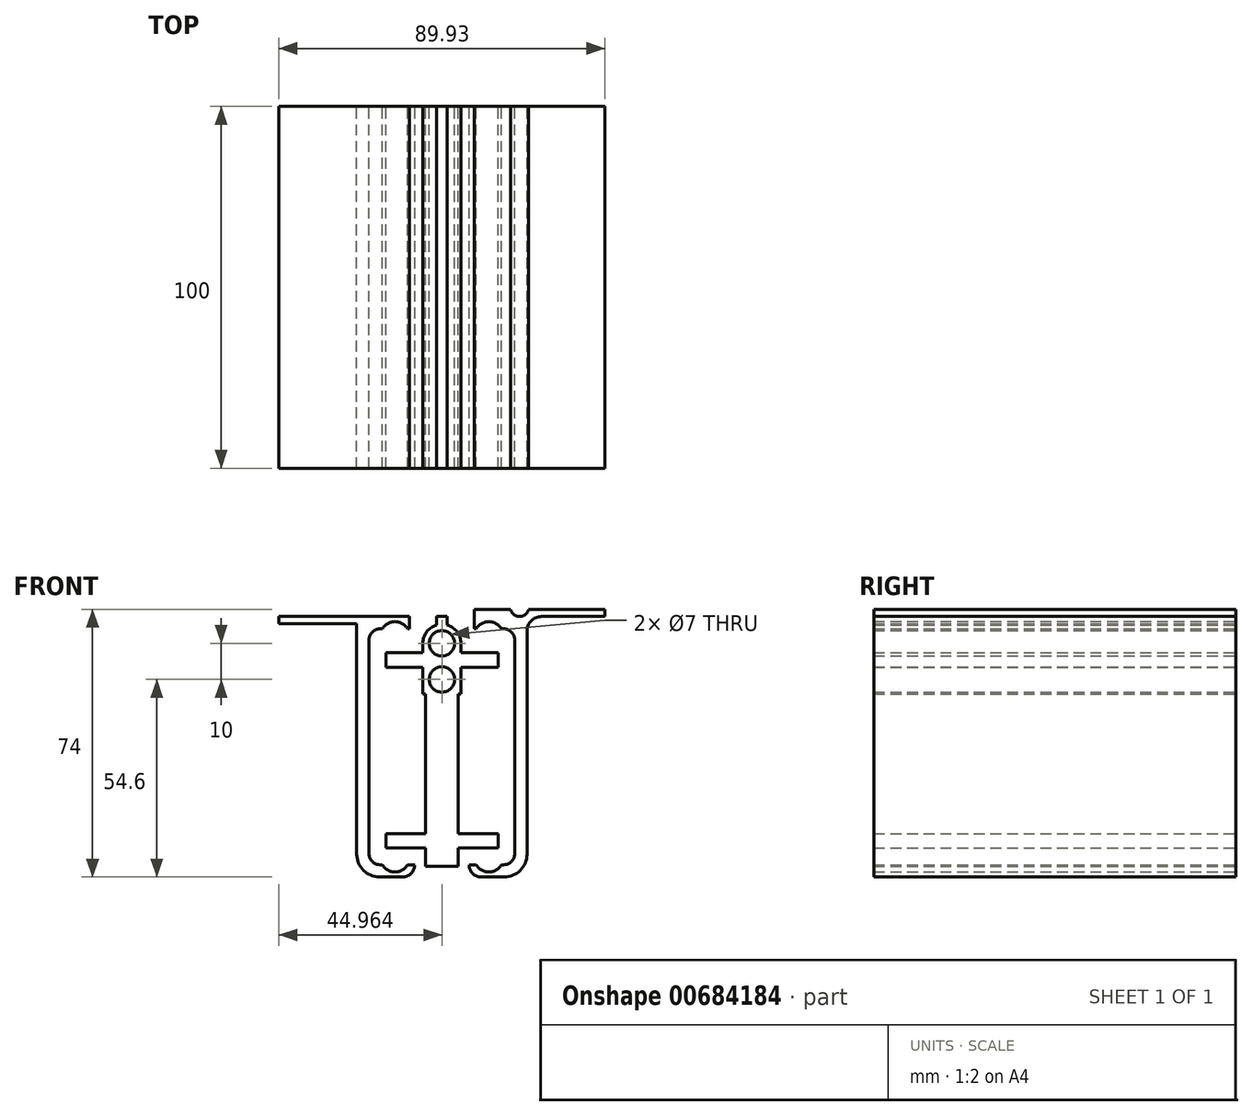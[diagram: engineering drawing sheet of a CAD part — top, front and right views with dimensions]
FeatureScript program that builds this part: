
annotation { "Feature Type Name" : "Feature", "Feature Type Description" : "" }
export const myFeature = defineFeature(function(context is Context, id is Id, definition is map)
    precondition{}
    {
        {
            var Q0;
            Q0=qCreatedBy(makeId("Front.planeOp"),FACE);
            var sketch = newSketch(context, id + "F0", { "sketchPlane" : qUnion([Q0])});
            skLineSegment(sketch, "E0", {"start": v(67.58, 68) * mm, "end": v(67.58, 6.3) * mm});
            skLineSegment(sketch, "E1", {"start": v(71.58, 72) * mm, "end": v(89.05, 72) * mm});
            skArc(sketch, "E2.filletArc", {"start": v(71.58, 72) * mm, "mid": v(68.76, 70.83) * mm, "end": v(67.58, 68) * mm});
            skLineSegment(sketch, "E3", {"start": v(61.18, 68.6) * mm, "end": v(53.05, 68.6) * mm});
            skLineSegment(sketch, "E4", {"start": v(61.18, 3.4) * mm, "end": v(51.58, 3.4) * mm});
            skLineSegment(sketch, "E5.0", {"start": v(64.18, 65.6) * mm, "end": v(64.18, 6.4) * mm});
            skArc(sketch, "E6.filletArc", {"start": v(61.18, 3.4) * mm, "mid": v(63.3, 4.28) * mm, "end": v(64.18, 6.4) * mm});
            skArc(sketch, "E7.filletArc", {"start": v(64.18, 65.6) * mm, "mid": v(63.3, 67.72) * mm, "end": v(61.18, 68.6) * mm});
            skLineSegment(sketch, "E8", {"start": v(61.28, 0) * mm, "end": v(54.98, 0) * mm});
            skPoint(sketch, "E9.visualSharp", {"position": v(67.58, 0) * mm});
            skArc(sketch, "E9.filletArc", {"start": v(61.28, 0) * mm, "mid": v(65.74, 1.85) * mm, "end": v(67.58, 6.3) * mm});
            skArc(sketch, "E10", {"start": v(60.51, 68.6) * mm, "mid": v(57.05, 70.6) * mm, "end": v(53.58, 68.6) * mm});
            skLineSegment(sketch, "E11", {"start": v(53.05, 68.6) * mm, "end": v(53.05, 74) * mm});
            skArc(sketch, "E12", {"start": v(63.05, 74) * mm, "mid": v(65.55, 72) * mm, "end": v(68.05, 74) * mm});
            skLineSegment(sketch, "E13", {"start": v(53.05, 74) * mm, "end": v(89.05, 74) * mm});
            skLineSegment(sketch, "E14", {"start": v(89.05, 72) * mm, "end": v(89.05, 74) * mm});
            skPoint(sketch, "E15", {"position": v(65.55, 72) * mm});
            skPoint(sketch, "E16", {"position": v(57.05, 70.6) * mm});
            skLineSegment(sketch, "E17", {"start": v(51.58, 3.4) * mm, "end": v(51.58, 3.4) * mm});
            skArc(sketch, "E18", {"start": v(53.58, 3.4) * mm, "mid": v(57.05, 1.4) * mm, "end": v(60.51, 3.4) * mm});
            skPoint(sketch, "E19", {"position": v(57.05, 1.4) * mm});
            skLineSegment(sketch, "E20", {"start": v(57.05, 66.6) * mm, "end": v(57.05, 5.3) * mm, "construction": true});
            skPoint(sketch, "E21.visualSharp", {"position": v(51.58, 0) * mm});
            skArc(sketch, "E21.filletArc", {"start": v(51.58, 3.4) * mm, "mid": v(52.58, 1) * mm, "end": v(54.98, 0) * mm});
            skLineSegment(sketch, "E22", {"start": v(44.08, 80.45) * mm, "end": v(44.08, 38.77) * mm, "construction": true});
            skLineSegment(sketch, "E23.MirrorCS", {"start": v(23.98, 65.6) * mm, "end": v(23.98, 6.4) * mm});
            skArc(sketch, "E24.MirrorCS", {"start": v(23.98, 65.6) * mm, "mid": v(24.86, 67.72) * mm, "end": v(26.98, 68.6) * mm});
            skArc(sketch, "E25.MirrorCS", {"start": v(26.98, 3.4) * mm, "mid": v(24.86, 4.28) * mm, "end": v(23.98, 6.4) * mm});
            skArc(sketch, "E26.MirrorCS", {"start": v(27.66, 68.6) * mm, "mid": v(31.12, 70.6) * mm, "end": v(34.58, 68.6) * mm});
            skLineSegment(sketch, "E27.MirrorCS", {"start": v(26.98, 68.6) * mm, "end": v(35.12, 68.6) * mm});
            skLineSegment(sketch, "E28.MirrorCS", {"start": v(26.98, 3.4) * mm, "end": v(36.58, 3.4) * mm});
            skArc(sketch, "E29.MirrorCS", {"start": v(34.58, 3.4) * mm, "mid": v(31.12, 1.4) * mm, "end": v(27.66, 3.4) * mm});
            skArc(sketch, "E30.MirrorCS", {"start": v(36.58, 3.4) * mm, "mid": v(35.59, 1) * mm, "end": v(33.18, 0) * mm});
            skLineSegment(sketch, "E31.MirrorCS", {"start": v(26.88, 0) * mm, "end": v(33.18, 0) * mm});
            skArc(sketch, "E32.MirrorCS", {"start": v(26.88, 0) * mm, "mid": v(22.43, 1.85) * mm, "end": v(20.58, 6.3) * mm});
            skLineSegment(sketch, "E33", {"start": v(20.58, 6.3) * mm, "end": v(20.58, 70) * mm});
            skLineSegment(sketch, "E34", {"start": v(20.58, 70) * mm, "end": v(-0.88, 70) * mm});
            skLineSegment(sketch, "E35", {"start": v(-0.88, 70) * mm, "end": v(-0.88, 72) * mm});
            skLineSegment(sketch, "E36", {"start": v(-0.88, 72) * mm, "end": v(35.12, 72) * mm});
            skLineSegment(sketch, "E37", {"start": v(35.12, 72) * mm, "end": v(35.12, 68.6) * mm});
            skCircle(sketch, "E38", {"center": v(44.08, 64.6) * mm, "radius": 3.5 * mm});
            skCircle(sketch, "E39", {"center": v(44.08, 54.6) * mm, "radius": 3.5 * mm});
            skLineSegment(sketch, "E40.top", {"start": v(38.83, 50.6) * mm, "end": v(39.58, 50.6) * mm});
            skLineSegment(sketch, "E40.left", {"start": v(38.83, 64.6) * mm, "end": v(38.83, 62) * mm});
            skLineSegment(sketch, "E40.right", {"start": v(49.33, 64.6) * mm, "end": v(49.33, 62) * mm});
            skLineSegment(sketch, "E41.bottom", {"start": v(39.58, 3) * mm, "end": v(48.58, 3) * mm});
            skLineSegment(sketch, "E41.left", {"start": v(39.58, 3) * mm, "end": v(39.58, 8) * mm});
            skLineSegment(sketch, "E41.right", {"start": v(48.58, 3) * mm, "end": v(48.58, 8) * mm});
            skLineSegment(sketch, "E42.trimOffspring", {"start": v(48.58, 50.6) * mm, "end": v(49.33, 50.6) * mm});
            skCircle(sketch, "E43.0", {"center": v(44.08, 64.6) * mm, "radius": 5.25 * mm});
            skLineSegment(sketch, "E44.bottom", {"start": v(45.58, 72) * mm, "end": v(42.58, 72) * mm});
            skLineSegment(sketch, "E44.left", {"start": v(45.58, 72) * mm, "end": v(45.58, 69.63) * mm});
            skLineSegment(sketch, "E44.right", {"start": v(42.58, 72) * mm, "end": v(42.58, 69.63) * mm});
            skLineSegment(sketch, "E45.bottom", {"start": v(28.58, 8) * mm, "end": v(39.58, 8) * mm});
            skLineSegment(sketch, "E45.top", {"start": v(28.58, 12) * mm, "end": v(39.58, 12) * mm});
            skLineSegment(sketch, "E45.left", {"start": v(28.58, 8) * mm, "end": v(28.58, 12) * mm});
            skLineSegment(sketch, "E45.right", {"start": v(59.58, 8) * mm, "end": v(59.58, 12) * mm});
            skLineSegment(sketch, "E46.trimOffspring", {"start": v(48.58, 8) * mm, "end": v(59.58, 8) * mm});
            skLineSegment(sketch, "E47.trimOffspring", {"start": v(48.58, 12) * mm, "end": v(59.58, 12) * mm});
            skLineSegment(sketch, "E48.trimOffspring", {"start": v(39.58, 12) * mm, "end": v(39.58, 50.6) * mm});
            skLineSegment(sketch, "E49.trimOffspring", {"start": v(48.58, 12) * mm, "end": v(48.58, 50.6) * mm});
            skLineSegment(sketch, "E50.bottom", {"start": v(28.58, 58) * mm, "end": v(38.83, 58) * mm});
            skLineSegment(sketch, "E50.top", {"start": v(28.58, 62) * mm, "end": v(38.83, 62) * mm});
            skLineSegment(sketch, "E50.left", {"start": v(28.58, 58) * mm, "end": v(28.58, 62) * mm});
            skLineSegment(sketch, "E50.right", {"start": v(59.58, 58) * mm, "end": v(59.58, 62) * mm});
            skLineSegment(sketch, "E51.trimOffspring", {"start": v(49.33, 58) * mm, "end": v(59.58, 58) * mm});
            skLineSegment(sketch, "E52.trimOffspring", {"start": v(49.33, 62) * mm, "end": v(59.58, 62) * mm});
            skLineSegment(sketch, "E53.trimOffspring", {"start": v(38.83, 58) * mm, "end": v(38.83, 50.6) * mm});
            skLineSegment(sketch, "E54.trimOffspring", {"start": v(49.33, 58) * mm, "end": v(49.33, 50.6) * mm});
            skSolve(sketch);
        }
        {
            var Q0;
            Q0=makeQuery(id+"F0.imprint","IMPRINT",FACE,{"disambiguationData":[TD([[makeQuery(id+"F0.imprint","IMPRINT",EDGE,{"derivedFrom":sQuery(id+"F0.wireOp",EDGE,"E0")}),-1.0]])]});
            extrude(context, id + "F1", {"entities" : qUnion([Q0]), "depth" : 100 * mm, "offsetDistance" : 25 * mm});
        }
        {
            var Q0;
            Q0=makeQuery(id+"F0.imprint","IMPRINT",FACE,{"disambiguationData":[TD([[makeQuery(id+"F0.imprint","IMPRINT",EDGE,{"derivedFrom":sQuery(id+"F0.wireOp",EDGE,"E23.MirrorCS")}),-1.0]])]});
            var Q1;
            Q1=makeQuery(id+"F1.opExtrude","CAP_FACE",FACE,{"disambiguationData":[OSD([sQuery(id+"F0.wireOp",EDGE,"E0"),sQuery(id+"F0.wireOp",EDGE,"E1"),sQuery(id+"F0.wireOp",EDGE,"E2.filletArc"),sQuery(id+"F0.wireOp",EDGE,"E3"),sQuery(id+"F0.wireOp",EDGE,"E4"),sQuery(id+"F0.wireOp",EDGE,"E5.0"),sQuery(id+"F0.wireOp",EDGE,"E6.filletArc"),sQuery(id+"F0.wireOp",EDGE,"E7.filletArc"),sQuery(id+"F0.wireOp",EDGE,"E8"),sQuery(id+"F0.wireOp",EDGE,"E9.filletArc"),sQuery(id+"F0.wireOp",EDGE,"E10"),sQuery(id+"F0.wireOp",EDGE,"E11"),sQuery(id+"F0.wireOp",EDGE,"E12"),sQuery(id+"F0.wireOp",EDGE,"E13"),sQuery(id+"F0.wireOp",EDGE,"E14"),sQuery(id+"F0.wireOp",EDGE,"E18"),sQuery(id+"F0.wireOp",EDGE,"E21.filletArc")])],"isStart":false});
            extrude(context, id + "F2", {"entities" : qUnion([Q0]), "endBound" : BoundingType.UP_TO_SURFACE, "depth" : 100 * mm, "endBoundEntityFace" : qUnion([Q1]), "offsetDistance" : 25 * mm});
        }
        {
            var Q0;
            Q0=makeQuery(id+"F0.imprint","IMPRINT",FACE,{"disambiguationData":[TD([[makeQuery(id+"F0.imprint","IMPRINT",EDGE,{"derivedFrom":sQuery(id+"F0.wireOp",EDGE,"E39")}),-1.0]])]});
            var Q1;
            Q1=makeQuery(id+"F0.imprint","IMPRINT",FACE,{"disambiguationData":[TD([[makeQuery(id+"F0.imprint","IMPRINT",EDGE,{"derivedFrom":sQuery(id+"F0.wireOp",EDGE,"E38")}),-1.0]])]});
            var Q2;
            Q2=makeQuery(id+"F0.imprint","IMPRINT",FACE,{"disambiguationData":[TD([[makeQuery(id+"F0.imprint","IMPRINT",EDGE,{"derivedFrom":sQuery(id+"F0.wireOp",EDGE,"E44.bottom")}),1.0]])]});
            var Q3;
            Q3=makeQuery(id+"F1.opExtrude","CAP_FACE",FACE,{"disambiguationData":[OSD([sQuery(id+"F0.wireOp",EDGE,"E0"),sQuery(id+"F0.wireOp",EDGE,"E1"),sQuery(id+"F0.wireOp",EDGE,"E2.filletArc"),sQuery(id+"F0.wireOp",EDGE,"E3"),sQuery(id+"F0.wireOp",EDGE,"E4"),sQuery(id+"F0.wireOp",EDGE,"E5.0"),sQuery(id+"F0.wireOp",EDGE,"E6.filletArc"),sQuery(id+"F0.wireOp",EDGE,"E7.filletArc"),sQuery(id+"F0.wireOp",EDGE,"E8"),sQuery(id+"F0.wireOp",EDGE,"E9.filletArc"),sQuery(id+"F0.wireOp",EDGE,"E10"),sQuery(id+"F0.wireOp",EDGE,"E11"),sQuery(id+"F0.wireOp",EDGE,"E12"),sQuery(id+"F0.wireOp",EDGE,"E13"),sQuery(id+"F0.wireOp",EDGE,"E14"),sQuery(id+"F0.wireOp",EDGE,"E18"),sQuery(id+"F0.wireOp",EDGE,"E21.filletArc")])],"isStart":false});
            extrude(context, id + "F3", {"entities" : qUnion([Q0, Q1, Q2]), "endBound" : BoundingType.UP_TO_SURFACE, "depth" : 10 * mm, "endBoundEntityFace" : qUnion([Q3]), "offsetDistance" : 25 * mm});
        }
    });
